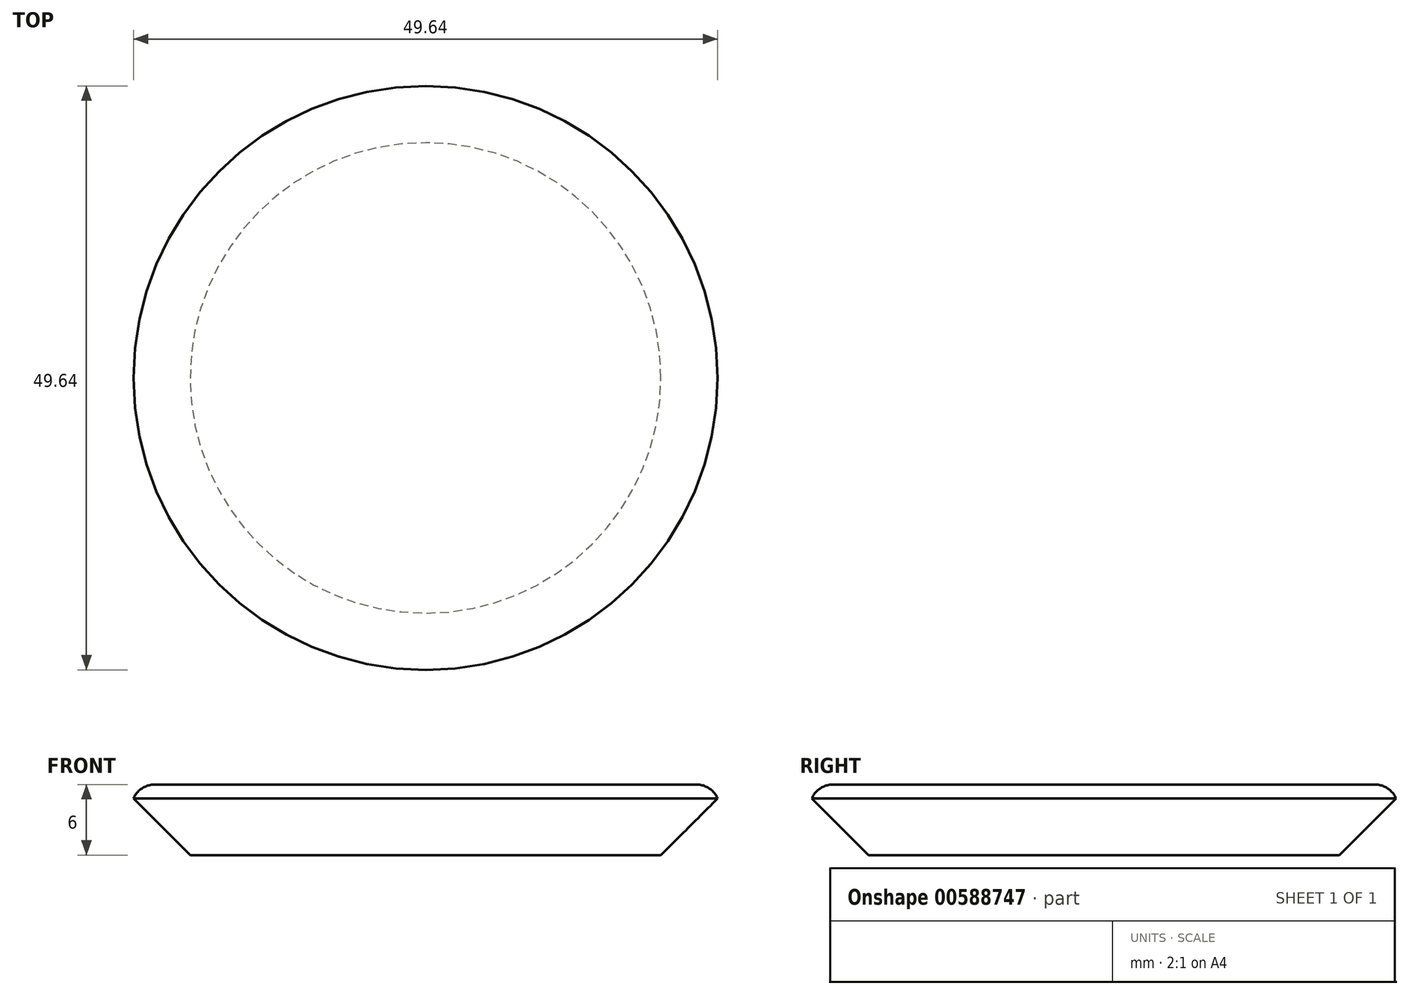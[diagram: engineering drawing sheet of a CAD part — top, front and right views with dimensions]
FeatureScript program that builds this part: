
annotation { "Feature Type Name" : "Feature", "Feature Type Description" : "" }
export const myFeature = defineFeature(function(context is Context, id is Id, definition is map)
    precondition{}
    {
        {
            var Q0;
            Q0=qCreatedBy(makeId("Top.planeOp"),FACE);
            var sketch = newSketch(context, id + "F0", { "sketchPlane" : qUnion([Q0])});
            skCircle(sketch, "E0", {"center": v(0, 0) * mm, "radius": 25 * mm});
            skSolve(sketch);
        }
        {
            var Q0;
            Q0=makeQuery(id+"F0.imprint","IMPRINT",FACE,{"disambiguationData":[TD([[makeQuery(id+"F0.imprint","IMPRINT",EDGE,{"derivedFrom":sQuery(id+"F0.wireOp",EDGE,"E0")}),1.0]])]});
            extrude(context, id + "F1", {"entities" : qUnion([Q0]), "depth" : 6 * mm, "offsetDistance" : 25 * mm, "symmetric" : true});
        }
        {
            var Q0;
            Q0=makeQuery(id+"F1.opExtrude","CAP_EDGE",EDGE,{"disambiguationData":[OSD([sQuery(id+"F0.wireOp",EDGE,"E0")])],"isStart":false});
            fillet(context, id + "F2", {"entities" : qUnion([Q0]), "radius" : 2 * mm, "tangentPropagation" : true, "allowEdgeOverflow" : false});
        }
        {
            var Q0;
            Q0=makeQuery(id+"F1.opExtrude","CAP_EDGE",EDGE,{"disambiguationData":[OSD([sQuery(id+"F0.wireOp",EDGE,"E0")])],"isStart":true});
            chamfer(context, id + "F3", {"entities" : qUnion([Q0]), "width" : 5 * mm, "tangentPropagation" : true});
        }
    });
